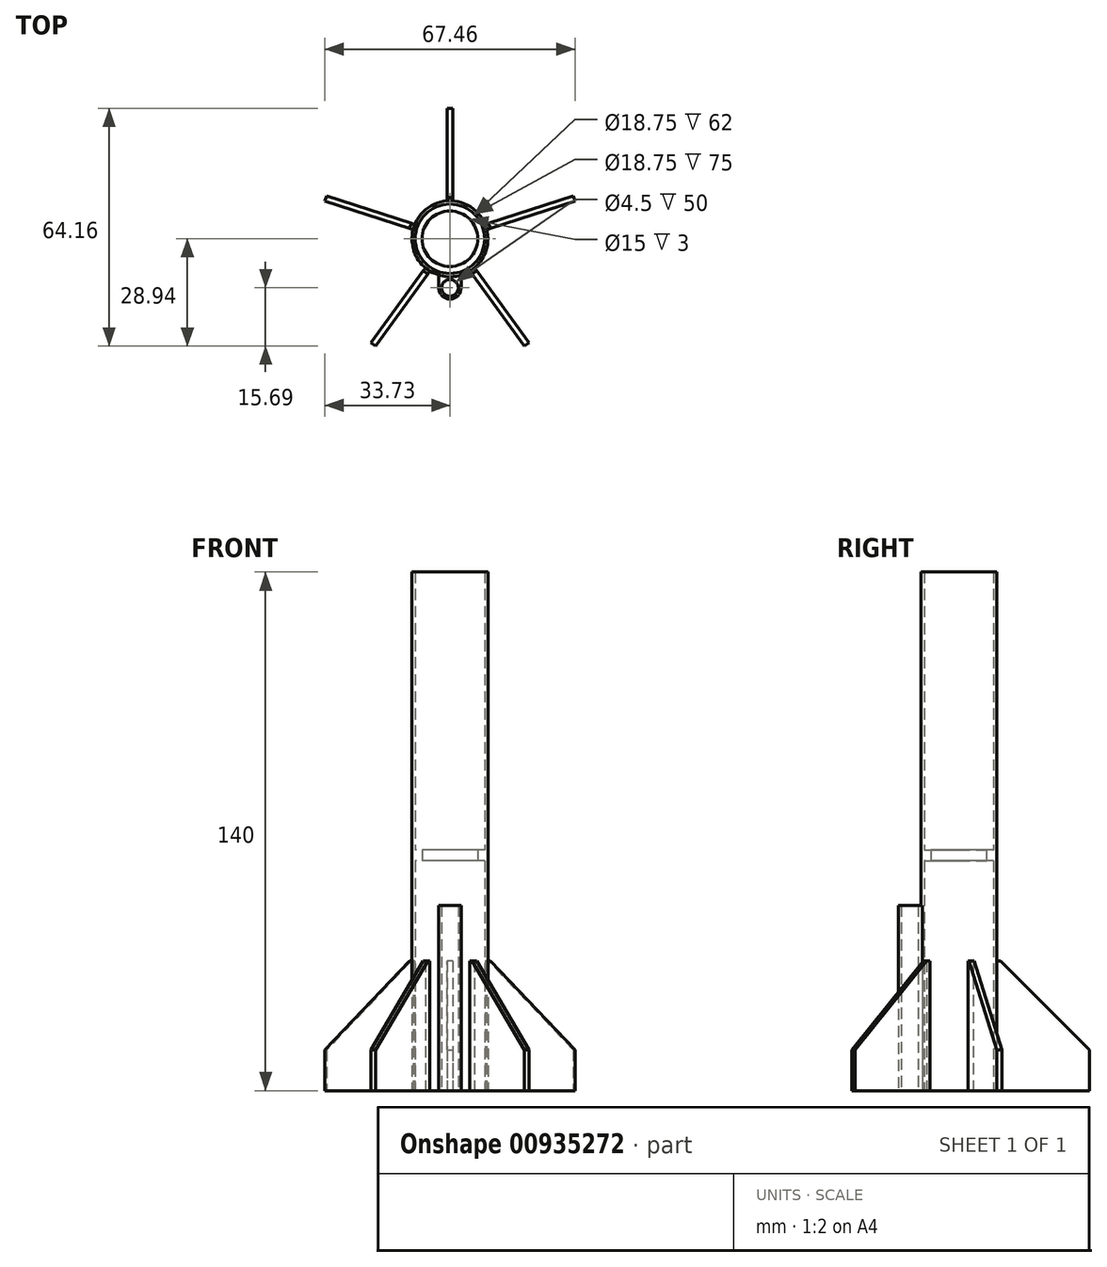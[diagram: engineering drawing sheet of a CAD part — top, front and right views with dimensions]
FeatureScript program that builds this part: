
annotation { "Feature Type Name" : "Feature", "Feature Type Description" : "" }
export const myFeature = defineFeature(function(context is Context, id is Id, definition is map)
    precondition{}
    {
        {
            var Q0;
            Q0=qCreatedBy(makeId("Top.planeOp"),FACE);
            var sketch = newSketch(context, id + "F0", { "sketchPlane" : qUnion([Q0])});
            skCircle(sketch, "E0", {"center": v(0, 0) * mm, "radius": 9.38 * mm});
            skCircle(sketch, "E1", {"center": v(0, 0) * mm, "radius": 10.25 * mm});
            skCircle(sketch, "E2", {"center": v(0, -13.25) * mm, "radius": 2.25 * mm});
            skCircle(sketch, "E3", {"center": v(0, -13.25) * mm, "radius": 3 * mm});
            skLineSegment(sketch, "E4", {"start": v(-3, -13.25) * mm, "end": v(-3, -9.8) * mm});
            skLineSegment(sketch, "E5", {"start": v(3, -13.25) * mm, "end": v(3, -9.8) * mm});
            skLineSegment(sketch, "E6.bottom", {"start": v(-0.75, 35.22) * mm, "end": v(0.75, 35.22) * mm});
            skLineSegment(sketch, "E6.left", {"start": v(-0.75, 35.22) * mm, "end": v(-0.75, 10.22) * mm});
            skLineSegment(sketch, "E6.right", {"start": v(0.75, 35.22) * mm, "end": v(0.75, 10.22) * mm});
            skCircle(sketch, "E7", {"center": v(0, 0) * mm, "radius": 7.5 * mm});
            skSolve(sketch);
        }
        {
            var Q0;
            Q0=makeQuery(id+"F0.imprint","IMPRINT",FACE,{"disambiguationData":[TD([[makeQuery(id+"F0.imprint","IMPRINT",EDGE,{"derivedFrom":sQuery(id+"F0.wireOp",EDGE,"E0")}),-1.0]])]});
            extrude(context, id + "F1", {"entities" : qUnion([Q0]), "depth" : 140 * mm, "offsetDistance" : 25 * mm});
        }
        {
            var Q0;
            Q0=makeQuery(id+"F0.imprint","IMPRINT",FACE,{"disambiguationData":[TD([[makeQuery(id+"F0.imprint","IMPRINT",EDGE,{"derivedFrom":sQuery(id+"F0.wireOp",EDGE,"E6.bottom")}),-1.0]])]});
            extrude(context, id + "F2", {"entities" : qUnion([Q0]), "operationType" : NewBodyOperationType.ADD, "depth" : 35 * mm, "offsetDistance" : 25 * mm});
        }
        {
            var Q0;
            Q0=makeQuery(id+"F2.opExtrude","CAP_EDGE",EDGE,{"disambiguationData":[OSD([sQuery(id+"F0.wireOp",EDGE,"E6.bottom")])],"isStart":false});
            chamfer(context, id + "F3", {"entities" : qUnion([Q0]), "width" : 24 * mm, "tangentPropagation" : true});
        }
        {
            var Q0;
            Q0=makeQuery(id+"F1.opExtrude","SWEPT_BODY",BODY,{"disambiguationData":[OSD([sQuery(id+"F0.wireOp",EDGE,"E0"),sQuery(id+"F0.wireOp",EDGE,"E1")])]});
            var Q1;
            Q1=makeQuery(id+"F1.opExtrude","CAP_EDGE",EDGE,{"disambiguationData":[OSD([sQuery(id+"F0.wireOp",EDGE,"E1")])],"isStart":false});
            circularPattern(context, id + "F4", {"entities" : qUnion([Q0]), "axis" : qUnion([Q1]), "angle" : 360 * degree, "instanceCount" : 5, "equalSpace" : true});
        }
        {
            var Q0;
            Q0=makeQuery(id+"F0.imprint","IMPRINT",FACE,{"disambiguationData":[TD([[makeQuery(id+"F0.imprint","IMPRINT",EDGE,{"derivedFrom":sQuery(id+"F0.wireOp",EDGE,"E2")}),-1.0]])]});
            var Q1;
            {var subQ0=sQuery(id+"F0.wireOp",EDGE,"E5");Q1=makeQuery(id+"F0.imprint","IMPRINT",FACE,{"disambiguationData":[TD([[makeQuery(id+"F0.imprint","IMPRINT",EDGE,{"derivedFrom":subQ0}),1.0]])]});}
            var Q2;
            {var subQ0=sQuery(id+"F0.wireOp",EDGE,"E4");Q2=makeQuery(id+"F0.imprint","IMPRINT",FACE,{"disambiguationData":[TD([[makeQuery(id+"F0.imprint","IMPRINT",EDGE,{"derivedFrom":subQ0}),-1.0]])]});}
            extrude(context, id + "F5", {"entities" : qUnion([Q0, Q1, Q2]), "operationType" : NewBodyOperationType.ADD, "depth" : 50 * mm, "offsetDistance" : 25 * mm});
        }
        {
            var Q0;
            Q0=makeQuery(id+"F0.imprint","IMPRINT",FACE,{"disambiguationData":[TD([[makeQuery(id+"F0.imprint","IMPRINT",EDGE,{"derivedFrom":sQuery(id+"F0.wireOp",EDGE,"E0")}),1.0]])]});
            extrude(context, id + "F6", {"entities" : qUnion([Q0]), "operationType" : NewBodyOperationType.ADD, "depth" : 65 * mm, "offsetDistance" : 25 * mm, "hasSecondDirection" : true, "secondDirectionOppositeDirection" : false, "secondDirectionDepth" : 62 * mm});
        }
    });
